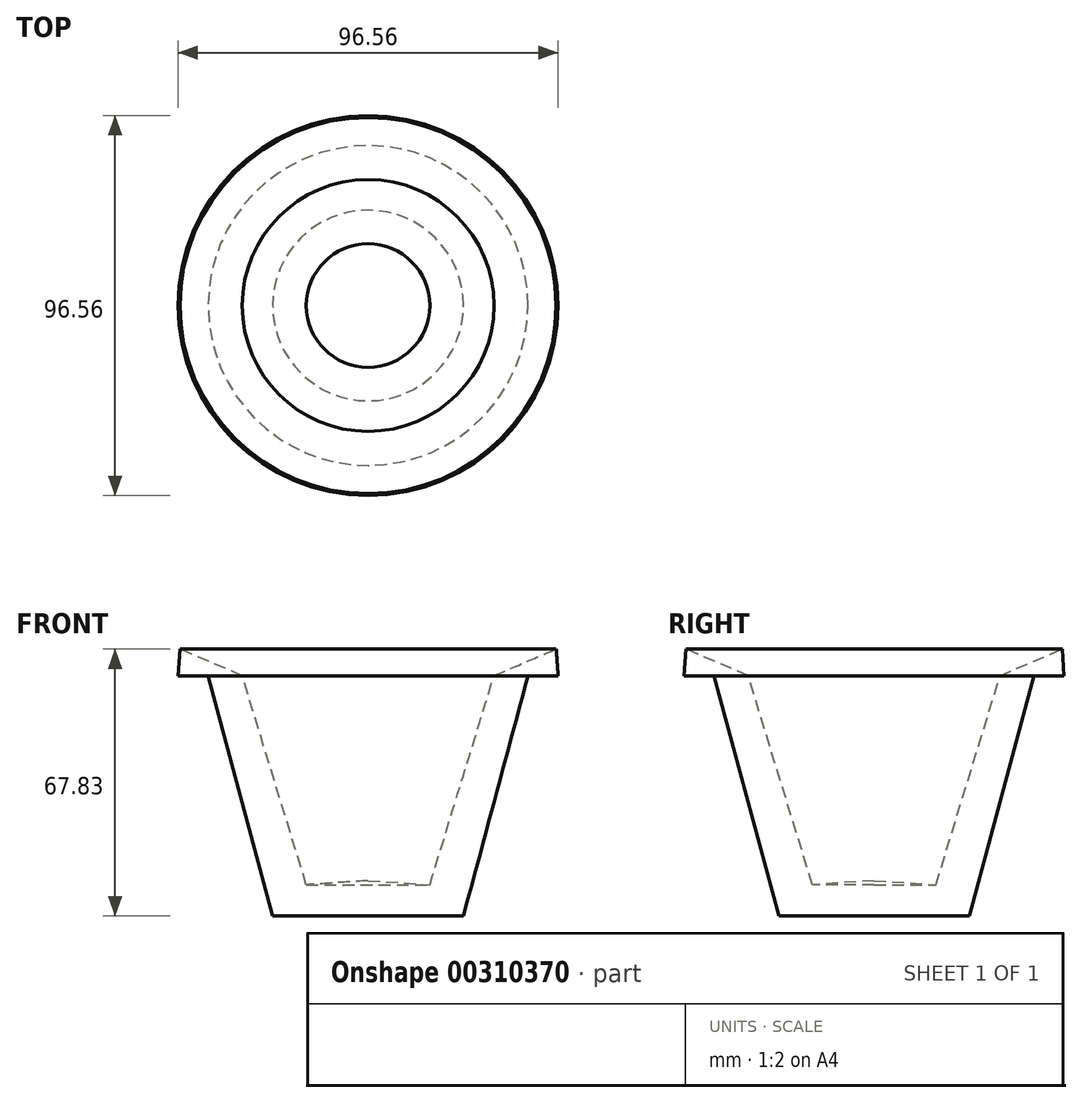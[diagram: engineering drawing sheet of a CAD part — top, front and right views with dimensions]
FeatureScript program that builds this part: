
annotation { "Feature Type Name" : "Feature", "Feature Type Description" : "" }
export const myFeature = defineFeature(function(context is Context, id is Id, definition is map)
    precondition{}
    {
        {
            var Q0;
            Q0=qCreatedBy(makeId("Front.planeOp"),FACE);
            var sketch = newSketch(context, id + "F0", { "sketchPlane" : qUnion([Q0])});
            skLineSegment(sketch, "E0", {"start": v(0, 0) * mm, "end": v(-24.22, 0) * mm});
            skLineSegment(sketch, "E1", {"start": v(-24.22, 0) * mm, "end": v(-40.62, 61.03) * mm});
            skLineSegment(sketch, "E2", {"start": v(-40.62, 61.03) * mm, "end": v(-48.28, 61.03) * mm});
            skLineSegment(sketch, "E3", {"start": v(-48.28, 61.03) * mm, "end": v(-47.78, 67.83) * mm});
            skLineSegment(sketch, "E4", {"start": v(-47.78, 67.83) * mm, "end": v(-31.98, 61.03) * mm});
            skLineSegment(sketch, "E5", {"start": v(-31.98, 61.03) * mm, "end": v(-15.7, 7.95) * mm});
            skLineSegment(sketch, "E6", {"start": v(-15.7, 7.95) * mm, "end": v(0, 8.97) * mm});
            skLineSegment(sketch, "E7", {"start": v(0, 8.97) * mm, "end": v(0, 0) * mm});
            skSolve(sketch);
        }
        {
            var Q0;
            Q0 = qSketchRegion(id + "F0", true);
            var Q1;
            Q1=sQuery(id+"F0.wireOp",EDGE,"E7");
            revolve(context, id + "F1", {"entities" : qUnion([Q0]), "axis" : qUnion([Q1]), "revolveType" : RevolveType.FULL});
        }
    });
